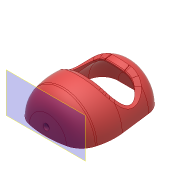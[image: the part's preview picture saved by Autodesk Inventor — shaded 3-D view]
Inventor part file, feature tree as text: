
AUTODESK INVENTOR PART (.ipt)
format: ipt  version: 2017 (Build 210142000, 142)  size: 610,816 bytes
history: native  units: mm
features: sketch x7, extrude x5, fillet x4, chamfer x3, revolve x1, shell x1, hole x1, plane x1, projected_geometry x1
ambient origin geometry x8: Origin, YZ Plane, XZ Plane, XY Plane, X Axis, Y Axis, Z Axis, Center Point
bodies: Solid1 (feature_tree)
feature tree (24):
  revolve  "Revolution1"  [1 undecoded]
  fillet  "Fillet1"  Radius=30.0mm
  chamfer  "Chamfer1"  Distance=10.0mm Angle=45.0deg
  fillet  "Fillet2"  Radius=20.0mm
  fillet  "Fillet3"  Radius=60.0mm
  extrude  "Extrusion1"  Depth=4.0mm
  shell  "Shell1"  Thickness=28.0mm
  extrude  "Extrusion2"  Depth=28.0mm
  chamfer  "Chamfer2"  Distance=100.0mm
  chamfer  "Chamfer3"  Distance=80.0mm
  extrude  "Extrusion3"  Depth=10.0mm TaperAngle=0.0deg
  extrude  "Extrusion4"  Depth=2.0mm
  hole  "Hole1"  [1 undecoded]
  plane  "Work Plane1"
  extrude  "Extrusion5"  Depth=3.0mm TaperAngle=45.0deg
  fillet  "Fillet4"  Radius=3.0mm
  sketch  "Sketch1"  dims[d0=40.0mm d1=80.0mm d2=30.0mm]
  sketch  "Sketch2"  dims[d3=90.0deg]
  sketch  "Sketch3"  dims[d4=20.0mm d5=10.0mm d6=20.0mm d7=45.0deg d8=20.0mm d9=60.0mm]
  sketch  "Sketch4"  dims[d10=10.0mm d11=0.0mm d12=4.0mm d13=28.0mm]
  sketch  "Sketch5"  dims[d14=28.0mm d15=28.0mm]
  sketch  "Sketch6"  dims[d16=46.0mm]
  projected_geometry  "Projected Loop1"
  sketch  "Sketch7"  dims[d17=13.0mm d18=100.0mm d19=0.0mm d20=80.0mm d21=10.0mm d22=0.0mm d24=120.0mm d25=80.0mm d26=3.0mm d27=2.0mm d28=45.0deg d29=3.0mm d30=2.0mm d31=45.0deg d32=6.0mm d33=12.0mm d34=14.0mm d35=0.0mm d36=8.0mm d37=24.0mm d38=4.0mm d39=0.0mm d40=8.0mm d41=3.5mm d42=6.0mm d43=4.0mm d44=2.0mm d45=90.0deg d46=8.0mm d47=20.594885mm d48=-9.5mm d49=6.0mm d50=4.0mm d51=0.0mm d52=2.0mm]
note: 2 required parameter values undecoded (feature->parameter linkage not recoverable at this tier; creation-order binding heuristic only, values carry confidence <= 0.55)